# Revit family: P210059AX-013_ASI2575GR_BSW
name_source: partatom
category: Specialty Equipment
units: mm (PartAtom-declared; Revit-internal decimal feet)

## family parameters
Always vertical = No
Cut with Voids When Loaded = No
Enable Cutting in Views = No
Maintain Annotation Orientation = No
Part Type = Normal
Room Calculation Point = No
Round Connector Dimension = Use Diameter
Shared = No
Work Plane-Based = No

## types (3) — shared parameters
Amps = 0 A
Back panel material = ARCAT - Metal - Aluminum
Clearance Material = ARCAT - Clearance
Default Elevation = 0"
Depth = 34 1/8"
Description = 36-inch Side-by-Side Refrigerator with Dual Pad External Ice and Water Dispenser
Display Material = ARCAT - Glass - Tempered - Black
Energy Guide = https://access.whirlpool.com Guide&sku=ASI2575GRB&language=EN
Family Name = Side by Side Refrigerator
Feature 1 = 21 Cu. Ft. Capacity.
Feature 2 = Dual Pad External Ice and Water Dispenser with EveryDrop™ Water Filter
Feature 3 = Electronic Temperature Controls
Glass Material = ARCAT - Glass - Tempered - Black
Height = 69 1/4"
Installation-Fabrication = https://access.whirlpool.com Instruction&sku=ASI2575GRB&language=EN
Manufacturer = Amana
Screw Material = ARCAT - Metal - Steel - Stainless
Voltage = 0 V
Width = 35 7/8"

## per-type parameters (varying)
| type | Accent Material | Body Material | Display Panel Material | Door Material | Handle Material | Tap Material | Tap Support Material |
| ASI2575GRS | ARCAT - Plastic - Gray | ARCAT - Metal - Steel - Gray | ARCAT - Glass - Tempered - Black | ARCAT - Metal - Steel - Stainless | ARCAT - Metal - Steel - Stainless | ARCAT - Plastic - Black | ARCAT - Plastic - Black |
| ASI2575GRW | ARCAT - Plastic - White | ARCAT - Metal - Steel - White | ARCAT - Plastic - White | ARCAT - Metal - Steel - White | ARCAT - Metal - Steel - White | ARCAT - Plastic - White | ARCAT - Plastic - White |
| ASI2575GRB | ARCAT - Metal - Steel - Black | ARCAT - Metal - Steel - Black | ARCAT - Plastic - Black | ARCAT - Metal - Steel - Black | ARCAT - Metal - Steel - Black | ARCAT - Plastic - Black | ARCAT - Plastic - Black |

note: column(s) folded — value = type name in every type: Model

## geometry (parser evidence)
native form markers: Sweep x6
no freeform markers — native parametric forms only
